# Revit family: MF_50_VO_804_D
name_source: partatom
category: Mechanical Equipment
revit_build: Autodesk Revit 2018 (Build: 20170223_1515(x64)
units: mm (PartAtom-declared; Revit-internal decimal feet)

## family parameters
Always vertical = Yes
Cut with Voids When Loaded = No
Part Type = Normal
Room Calculation Point = No
Round Connector Dimension = Use Radius
Shared = No
Work Plane-Based = No

## types (1)
- MF VO 804 D
    Cable = Neoprene
    Cable Length (m) = As Per Specification
    Cable Type (H07RN-F) = F4G1.0
    Capacity (m3/hr) = 35 m³
    Description = Compact submersible pumps with large solids passage for the reliable and effective dewatering of buildings and sites.
    Fasteners = Stainless steel 1.4401 (AISI 316)
    Handle = Handle
    Head (m) = 16 mm  [stored 0.0524934 ft]
    Impeller = Polyamide
    Manufacturer = Sulzer
    Model = Light Wastewater Pump Type ABS MF 804 VO
    Motor Housing = Cast Iron EN-GJL-250
    Motor Power (kW) = P1=2.40 P2=1.80
    Product Specification Link = https://www.sulzer.com
    Rated Current (A) = 4.1
    Rated Voltage (V) = 400 3~
    Rotor Shaft = Stainless steel 1.4021 (AISI 420)
    Speed (r/min) = 2900
    Upper Lid = Stainless steel 1.4301 (AISI 304)
    Volute = Cast Iron EN-GJL-250

note: [stored X ft] marks values corroborated as IEEE doubles in the binary element streams (Revit-internal decimal feet)

## geometry (parser evidence)
native form markers: Sweep x3
no freeform markers — native parametric forms only
